FCSTD DOCUMENT  (FreeCAD 0.20R29177 +426 (Git))
Label: RecogBoxPartialAssembly_v3
License: All rights reserved
LicenseURL: https://en.wikipedia.org/wiki/All_rights_reserved
objects: App::DocumentObjectGroup×4, App::Link×3, PartDesign::CoordinateSystem×1, App::FeaturePython×1, App::Part×1, Part::FeaturePython×1, App::AnnotationLabel×1
note: 2 computed .brp shape members not serialized (recipe doc carries the construction recipe); baked Part::Feature solids carry a one-line shape summary decoded from their .brp
EXTERNAL_REF file=ImageRecogBox-v3-cutinparts.FCStd obj=LCS_2
EXTERNAL_REF file=ImageRecogBox-v3-cutinparts.FCStd obj=Body
EXTERNAL_REF file=ImageRecogBox-v3-cutinparts.FCStd obj=LCS_6
EXTERNAL_REF file=left_handle.FCStd obj=LCS_1
EXTERNAL_REF file=left_handle.FCStd obj=Body
EXTERNAL_REF file=ImageRecogBox-v3-cutinparts.FCStd obj=LCS_5
EXTERNAL_REF file=right_handle.FCStd obj=LCS_1
EXTERNAL_REF file=right_handle.FCStd obj=Body

FEATURE [App::DocumentObjectGroup] Parts
FEATURE [PartDesign::CoordinateSystem] LCS_Origin
  AttacherType = Attacher::AttachEngine3D
  MapMode = 2
  Support = -> [X_Axis]
FEATURE [App::DocumentObjectGroup] Constraints
FEATURE [App::FeaturePython] Variables  # WARN: FeaturePython — macro-defined, semantics opaque (R4)
  Type = App::PropertyContainer
FEATURE [App::DocumentObjectGroup] Configurations
FEATURE [App::Link] ImageRecogBox_body  label="ImageRecogBox-body"
  AttachedBy = #LCS_2
  AttachedTo = Parent Assembly#LCS_Origin
  LinkedObject = -> <external ImageRecogBox-v3-cutinparts.FCStd>#Body
  SolverId = Asm4EE
  expr: Placement = LCS_Origin.Placement * AttachmentOffset * ImageRecogBox_v3_cutinparts#LCS_2.Placement ^ -1
FEATURE [App::Link] Body
  AttachedBy = #LCS_1
  AttachedTo = ImageRecogBox_body#LCS_6
  LinkPlacement = pos=(-121.969,50.5,41.5) rot=(0,0,-1;1.5708rad)
  LinkedObject = -> <external left_handle.FCStd>#Body
  Placement = pos=(-121.969,50.5,41.5) rot=(0,0,-1;1.5708rad)
  SolverId = Asm4EE
  expr: Placement = ImageRecogBox_body.Placement * ImageRecogBox_v3_cutinparts#LCS_6.Placement * AttachmentOffset * left_handle#LCS_1.Placement ^ -1
FEATURE [App::Link] Body001
  AttachedBy = #LCS_1
  AttachedTo = ImageRecogBox_body#LCS_5
  LinkPlacement = pos=(17.25,130.878,41.5) rot=(0,0,-1;0.523599rad)
  LinkedObject = -> <external right_handle.FCStd>#Body
  Placement = pos=(17.25,130.878,41.5) rot=(0,0,-1;0.523599rad)
  SolverId = Asm4EE
  expr: Placement = ImageRecogBox_body.Placement * ImageRecogBox_v3_cutinparts#LCS_5.Placement * AttachmentOffset * right_handle#LCS_1.Placement ^ -1
FEATURE [App::Part] Assembly
  AssemblyType = Part::Link
  Group = -> [LCS_Origin,Constraints,Variables,Configurations,ImageRecogBox_body,Body,Body001]
  Origin = -> Origin
  Type = Assembly
FEATURE [Part::FeaturePython] DistPoints  # WARN: FeaturePython — macro-defined, semantics opaque (R4)
FEATURE [App::AnnotationLabel] MeasureLbl
  BasePosition = (-78.861,136.591,41.5)
  LabelText = D = 33,36 mm
  TextPosition = (0,0,0)
FEATURE [App::DocumentObjectGroup] Measures
  Group = -> [DistPoints,MeasureLbl]

RESOLVED EXTERNAL PARTS (link-assembly join: the EXTERNAL_REF files above that resolve inside this repo's crawl, each included once):
---- part ImageRecogBox-v3-cutinparts.FCStd = doc fcstd_85f84b476632 ----
FCSTD DOCUMENT  (FreeCAD 0.20R29177 +426 (Git))
Label: ImageRecogBox-v3-cutinparts
License: All rights reserved
LicenseURL: http://en.wikipedia.org/wiki/All_rights_reserved
objects: Sketcher::SketchObject×16, PartDesign::Pad×9, PartDesign::CoordinateSystem×6, PartDesign::Hole×4, PartDesign::Pocket×3, PartDesign::Chamfer×2, App::DocumentObjectGroup×1, PartDesign::Body×1
note: 59 computed .brp shape members not serialized (recipe doc carries the construction recipe); baked Part::Feature solids carry a one-line shape summary decoded from their .brp

FEATURE [Sketcher::SketchObject] Sketch
  FullyConstrained = true
  MapMode = 5
  Support = -> [XY_Plane]
  sketch-geometry (14):
    g0: LineSegment StartX=86.6025 StartY=50 StartZ=0 EndX=0 EndY=100 EndZ=0
    g1: LineSegment StartX=4.3e-15 StartY=100 StartZ=0 EndX=-86.6025 EndY=50 EndZ=0
    g2: LineSegment StartX=-86.6025 StartY=50 StartZ=0 EndX=-86.6025 EndY=-50 EndZ=0
    g3: LineSegment StartX=-86.6025 StartY=-50 StartZ=0 EndX=0 EndY=-100 EndZ=0
    g4: LineSegment StartX=0 StartY=-100 StartZ=0 EndX=86.6025 EndY=-50 EndZ=0
    g5: LineSegment StartX=86.6025 StartY=-50 StartZ=0 EndX=86.6025 EndY=50 EndZ=0
    g6: Circle CenterX=0 CenterY=0 CenterZ=0 NormalX=0 NormalY=0 NormalZ=1 AngleXU=0 Radius=100
    g7: LineSegment StartX=87.4686 StartY=-50.5 StartZ=0 EndX=87.4686 EndY=50.5 EndZ=0
    g8: LineSegment StartX=87.4686 StartY=50.5 StartZ=0 EndX=-1.42e-14 EndY=101 EndZ=0
    g9: LineSegment StartX=-1.48e-14 StartY=101 StartZ=0 EndX=-87.4686 EndY=50.5 EndZ=0
    g10: LineSegment StartX=-87.4686 StartY=50.5 StartZ=0 EndX=-87.4686 EndY=-50.5 EndZ=0
    g11: LineSegment StartX=-87.4686 StartY=-50.5 StartZ=0 EndX=0 EndY=-101 EndZ=0
    g12: LineSegment StartX=0 StartY=-101 StartZ=0 EndX=87.4686 EndY=-50.5 EndZ=0
    g13: Circle CenterX=0 CenterY=0 CenterZ=0 NormalX=0 NormalY=0 NormalZ=1 AngleXU=0 Radius=101
  constraints (33):
    c: Coincident(g0,g1)
    c: Coincident(g1,g2)
    c: Coincident(g2,g3)
    c: Coincident(g3,g4)
    c: Coincident(g4,g5)
    c: Coincident(g5,g0)
    c: Equal(g0, g1-g5) x5
    c: PointOnObject(g0,g6)
    c: PointOnObject(g1,g6)
    c: PointOnObject(g2,g6)
    c: PointOnObject(g3,g6)
    c: PointOnObject(g4,g6)
    c: PointOnObject(g5,g6)
    c: Coincident(g6,g-1)
    c: Vertical(g5)
    c: Coincident(g7,g8)
    c: Coincident(g8,g9)
    c: Coincident(g9,g10)
    c: Coincident(g10,g11)
    c: Coincident(g11,g12)
    c: Coincident(g12,g7)
    c: Equal(g7, g8-g12) x5
    c: PointOnObject(g7,g13)
    c: PointOnObject(g8,g13)
    c: PointOnObject(g9,g13)
    c: PointOnObject(g10,g13)
    c: PointOnObject(g11,g13)
    c: PointOnObject(g12,g13)
    c: Coincident(g13,g6)
    c: Vertical(g7)
    c: Diameter(g6) = 200
    c: DistanceY(g5,g5) = 100
    c: Diameter(g13) = 202
FEATURE [PartDesign::Pad] Pad
  Direction = (0,0,1)
  Length = 150
  Length2 = 10
  Profile = -> Sketch
  ReferenceAxis = -> Sketch [N_Axis]
  Type = 0
FEATURE [Sketcher::SketchObject] Sketch001
  ExternalGeometry = -> [Pad]
  FullyConstrained = true
  MapMode = 5
  Placement = pos=(0,0,0) rot=(1,0,0;3.14159rad)
  Support = -> [Pad]
  sketch-geometry (4):
    g0: LineSegment StartX=103.603 StartY=0 StartZ=0 EndX=86.6025 EndY=0 EndZ=0
    g1: LineSegment StartX=86.6025 StartY=0 StartZ=0 EndX=86.6025 EndY=-10 EndZ=0
    g2: LineSegment StartX=86.6025 StartY=-10 StartZ=0 EndX=103.603 EndY=-10 EndZ=0
    g3: LineSegment StartX=103.603 StartY=-10 StartZ=0 EndX=103.603 EndY=0 EndZ=0
  constraints (12):
    c: Coincident(g0,g1)
    c: Coincident(g1,g2)
    c: Coincident(g2,g3)
    c: Coincident(g3,g0)
    c: Horizontal(g0)
    c: Horizontal(g2)
    c: Vertical(g1)
    c: Vertical(g3)
    c: PointOnObject(g1,g-3)
    c: DistanceX(g2,g2) = 17
    c: DistanceY(g3,g3) = 10
    c: PointOnObject(g0,g-1)
FEATURE [PartDesign::Pad] Pad001
  BaseFeature = -> Pad
  Direction = (0,0,-1)
  Length = 25
  Length2 = 10
  Profile = -> Sketch001
  ReferenceAxis = -> Sketch001 [N_Axis]
  Type = 0
FEATURE [Sketcher::SketchObject] Sketch002
  ExternalGeometry = -> [Pad001]
  FullyConstrained = true
  MapMode = 5
  Placement = pos=(0,0,-25) rot=(1,0,0;3.14159rad)
  Support = -> [Pad001]
  sketch-geometry (4):
    g0: LineSegment StartX=103.603 StartY=-10 StartZ=0 EndX=73.6025 EndY=-10 EndZ=0
    g1: LineSegment StartX=73.6025 StartY=-10 StartZ=0 EndX=73.6025 EndY=50 EndZ=0
    g2: LineSegment StartX=73.6025 StartY=50 StartZ=0 EndX=103.603 EndY=50 EndZ=0
    g3: LineSegment StartX=103.603 StartY=50 StartZ=0 EndX=103.603 EndY=-10 EndZ=0
  constraints (11):
    c: Coincident(g0,g1)
    c: Coincident(g2,g3)
    c: Coincident(g3,g0)
    c: Horizontal(g0)
    c: Vertical(g3)
    c: Coincident(g0,g-4)
    c: Coincident(g2,g1)
    c: Horizontal(g2)
    c: Horizontal(g2,g-6)
    c: Vertical(g1)
    c: DistanceX(g0,g0) = 30
FEATURE [PartDesign::Pad] Pad002
  BaseFeature = -> Pad001
  Direction = (0,0,-1)
  Length = 8
  Length2 = 10
  Profile = -> Sketch002
  ReferenceAxis = -> Sketch002 [N_Axis]
  Type = 0
FEATURE [Sketcher::SketchObject] Sketch003
  ExternalGeometry = -> [Pad002]
  FullyConstrained = true
  MapMode = 5
  Placement = pos=(0,0,-25) rot=(0,0,1;0rad)
  Support = -> [Pad002]
  sketch-geometry (6):
    g0: LineSegment StartX=76.1025 StartY=-8 StartZ=0 EndX=89.1025 EndY=-8 EndZ=0
    g1: LineSegment StartX=89.1025 StartY=-8 StartZ=0 EndX=89.1025 EndY=-32 EndZ=0
    g2: LineSegment StartX=89.1025 StartY=-32 StartZ=0 EndX=76.1025 EndY=-32 EndZ=0
    g3: LineSegment StartX=76.1025 StartY=-32 StartZ=0 EndX=76.1025 EndY=-8 EndZ=0
    g4: GeomPoint X=82.6025 Y=-20 Z=0
    g5: GeomPoint X=88.6025 Y=-20 Z=0
  constraints (14):
    c: Coincident(g0,g1)
    c: Coincident(g1,g2)
    c: Coincident(g2,g3)
    c: Coincident(g3,g0)
    c: Horizontal(g0)
    c: Horizontal(g2)
    c: Vertical(g1)
    c: Vertical(g3)
    c: DistanceY(g1,g1) = 24
    c: DistanceX(g2,g2) = 13
    c: Symmetric(g1,g0,g4)
    c: Symmetric(g-5,g-3,g5)
    c: DistanceX(g4,g5) = 6
    c: Horizontal(g5,g4)
FEATURE [PartDesign::Pocket] Pocket
  BaseFeature = -> Pad002
  Direction = (0,0,-1)
  Length = 19
  Length2 = 5
  Profile = -> Sketch003
  ReferenceAxis = -> Sketch003 [N_Axis]
  Type = 1
FEATURE [Sketcher::SketchObject] Sketch004
  ExternalGeometry = -> [Pocket]
  FullyConstrained = false
  MapMode = 5
  Placement = pos=(0,0,-25) rot=(0,0,1;0rad)
  Support = -> [Pocket]
  sketch-geometry (5):
    g0: GeomPoint X=82.6025 Y=-6.3796 Z=0
    g1: GeomPoint X=82.6025 Y=-33.3796 Z=0
    g2: Circle CenterX=82.6025 CenterY=-6.3796 CenterZ=0 NormalX=0 NormalY=0 NormalZ=1 AngleXU=0 Radius=1
    g3: Circle CenterX=82.6025 CenterY=-33.3796 CenterZ=0 NormalX=0 NormalY=0 NormalZ=1 AngleXU=0 Radius=1
    g4: GeomPoint X=82.6025 Y=-20 Z=0
  constraints (8):
    c: DistanceY(g1,g0) = 27
    c: Coincident(g2,g0)
    c: Coincident(g3,g1)
    c: Equal(g3,g2)
    c: Diameter(g2) = 2
    c: Symmetric(g-6,g-5,g4)
    c: Vertical(g2,g3)
    c: Vertical(g3,g4)
FEATURE [PartDesign::Hole] Hole
  BaseFeature = -> Pocket
  CustomThreadClearance = 0
  Depth = 25
  DepthType = 0
  Diameter = 1.6
  DrillForDepth = false
  DrillPoint = 1
  DrillPointAngle = 118
  HoleCutCountersinkAngle = 90
  HoleCutCustomValues = false
  HoleCutDepth = 0
  HoleCutDiameter = 6.1
  HoleCutType = 0
  ModelThread = false
  Profile = -> Sketch004
  Tapered = false
  TaperedAngle = 90
  ThreadClass = 0
  ThreadDepth = 25
  ThreadDepthType = 0
  ThreadDirection = 0
  ThreadFit = 0
  ThreadSize = 6
  ThreadType = 1
  Threaded = true
  UseCustomThreadClearance = false
FEATURE [PartDesign::CoordinateSystem] LCS_1
  AttacherType = Attacher::AttachEngine3D
  MapMode = 45
  Placement = pos=(82.6025,-6.3796,-25) rot=(0,0,1;0rad)
  Support = -> [Hole]
FEATURE [PartDesign::CoordinateSystem] LCS_2  label="LCS_origin"
  AttacherType = Attacher::AttachEngine3D
FEATURE [PartDesign::Chamfer] Chamfer
  Angle = 45
  Base = -> Hole [Edge4]
  BaseFeature = -> Hole
  ChamferType = 0
  FlipDirection = false
  Size = 16
  Size2 = 1
  SupportTransform = false
  UseAllEdges = false
FEATURE [PartDesign::Chamfer] Chamfer001
  Angle = 45
  Base = -> Chamfer [Edge12,Edge49]
  BaseFeature = -> Chamfer
  ChamferType = 0
  FlipDirection = false
  Size = 3
  Size2 = 1
  SupportTransform = false
  UseAllEdges = false
FEATURE [Sketcher::SketchObject] Sketch005
  ExternalGeometry = -> [Chamfer001]
  FullyConstrained = true
  MapMode = 5
  Placement = pos=(0,0,0) rot=(1,0,0;3.14159rad)
  Support = -> [Chamfer001]
  sketch-geometry (8):
    g0: LineSegment StartX=86.6025 StartY=-10 StartZ=0 EndX=86.6025 EndY=-50 EndZ=0
    g1: LineSegment StartX=86.6025 StartY=-50 StartZ=0 EndX=0 EndY=-100 EndZ=0
    g2: LineSegment StartX=0 StartY=-100 StartZ=0 EndX=-86.6025 EndY=-50 EndZ=0
    g3: LineSegment StartX=-86.6025 StartY=-50 StartZ=0 EndX=-87.4686 EndY=-50.5 EndZ=0
    g4: LineSegment StartX=-87.4686 StartY=-50.5 StartZ=0 EndX=-1.42e-14 EndY=-101 EndZ=0
    g5: LineSegment StartX=-1.42e-14 StartY=-101 StartZ=0 EndX=87.4686 EndY=-50.5 EndZ=0
    g6: LineSegment StartX=87.4686 StartY=-50.5 StartZ=0 EndX=87.4686 EndY=-10 EndZ=0
    g7: LineSegment StartX=87.4686 StartY=-10 StartZ=0 EndX=86.6025 EndY=-10 EndZ=0
  constraints (16):
    c: Coincident(g-7,g0)
    c: Coincident(g0,g-7)
    c: Coincident(g0,g1)
    c: Coincident(g1,g-4)
    c: Coincident(g1,g2)
    c: Coincident(g2,g-3)
    c: Coincident(g2,g3)
    c: Coincident(g3,g-5)
    c: Coincident(g3,g4)
    c: Coincident(g4,g-6)
    c: Coincident(g4,g5)
    c: Coincident(g5,g-8)
    c: Coincident(g5,g6)
    c: Coincident(g6,g-8)
    c: Coincident(g6,g7)
    c: Coincident(g7,g0)
FEATURE [PartDesign::Pad] Pad003
  BaseFeature = -> Chamfer001
  Direction = (0,0,-1)
  Length = 12
  Length2 = 10
  Profile = -> Sketch005
  ReferenceAxis = -> Sketch005 [N_Axis]
  Type = 0
FEATURE [Sketcher::SketchObject] Sketch006
  ExternalGeometry = -> [Pad003]
  FullyConstrained = true
  MapMode = 5
  Placement = pos=(87.4686,0,0) rot=(0.57735,0.57735,0.57735;2.0944rad)
  Support = -> [Pad003]
  sketch-geometry (6):
    g0: GeomPoint X=30.25 Y=-12 Z=0
    g1: LineSegment StartX=37.75 StartY=-12 StartZ=0 EndX=22.75 EndY=-12 EndZ=0
    g2: LineSegment StartX=22.75 StartY=-12 StartZ=0 EndX=22.75 EndY=38 EndZ=0
    g3: LineSegment StartX=22.75 StartY=38 StartZ=0 EndX=37.75 EndY=38 EndZ=0
    g4: LineSegment StartX=37.75 StartY=38 StartZ=0 EndX=37.75 EndY=-12 EndZ=0
    g5: GeomPoint X=22.75 Y=13 Z=0
  constraints (13):
    c: Symmetric(g-3,g-3,g0)
    c: Coincident(g1,g2)
    c: Coincident(g2,g3)
    c: Coincident(g3,g4)
    c: Coincident(g4,g1)
    c: Horizontal(g1)
    c: Horizontal(g3)
    c: Vertical(g2)
    c: Vertical(g4)
    c: Symmetric(g1,g1,g0)
    c: DistanceX(g1,g1) = 15
    c: DistanceY(g4,g4) = 50
    c: Symmetric(g2,g1,g5)
FEATURE [PartDesign::Pad] Pad004
  BaseFeature = -> Pad003
  Direction = (1,0,0)
  Length = 10
  Length2 = 10
  Profile = -> Sketch006
  ReferenceAxis = -> Sketch006 [N_Axis]
  Type = 0
FEATURE [Sketcher::SketchObject] Sketch007
  ExternalGeometry = -> [Pad004]
  FullyConstrained = false
  MapMode = 5
  Placement = pos=(97.4686,0,0) rot=(0.57735,0.57735,0.57735;2.0944rad)
  Support = -> [Pad004]
  sketch-geometry (3):
    g0: Circle CenterX=30.25 CenterY=25.5 CenterZ=0 NormalX=0 NormalY=0 NormalZ=1 AngleXU=0 Radius=1.58506
    g1: GeomPoint X=22.75 Y=13 Z=0
    g2: Circle CenterX=30.25 CenterY=0.5 CenterZ=0 NormalX=0 NormalY=0 NormalZ=1 AngleXU=0 Radius=1.58506
  constraints (3):
    c: Symmetric(g-3,g-3,g1)
    c: Symmetric(g-4,g1,g0)
    c: Symmetric(g-4,g1,g2)
FEATURE [PartDesign::Hole] Hole001
  BaseFeature = -> Pad004
  CustomThreadClearance = 0
  Depth = 6
  DepthType = 0
  Diameter = 3.4
  DrillForDepth = false
  DrillPoint = 1
  DrillPointAngle = 118
  HoleCutCountersinkAngle = 90
  HoleCutCustomValues = false
  HoleCutDepth = 0
  HoleCutDiameter = 6.1
  HoleCutType = 0
  ModelThread = false
  Profile = -> Sketch007
  Tapered = false
  TaperedAngle = 90
  ThreadClass = 0
  ThreadDepth = 6
  ThreadDepthType = 0
  ThreadDirection = 0
  ThreadFit = 0
  ThreadSize = 9
  ThreadType = 1
  Threaded = false
  UseCustomThreadClearance = false
FEATURE [PartDesign::CoordinateSystem] LCS_3
  AttacherType = Attacher::AttachEngine3D
  MapMode = 11
  Placement = pos=(97.4686,30.25,25.5) rot=(0.57735,0.57735,0.57735;2.0944rad)
  Support = -> [Hole001]
FEATURE [App::DocumentObjectGroup] Measures
FEATURE [Sketcher::SketchObject] Sketch008
  ExternalGeometry = -> [Hole001]
  FullyConstrained = true
  MapMode = 5
  Placement = pos=(43.7343,75.75,0) rot=(0.186157,0.694747,0.694747;2.77349rad)
  Support = -> [Hole001]
  sketch-geometry (5):
    g0: GeomPoint X=-2.7e-15 Y=-12 Z=0
    g1: LineSegment StartX=-7.5 StartY=38 StartZ=0 EndX=7.5 EndY=38 EndZ=0
    g2: LineSegment StartX=7.5 StartY=38 StartZ=0 EndX=7.5 EndY=-12 EndZ=0
    g3: LineSegment StartX=7.5 StartY=-12 StartZ=0 EndX=-7.5 EndY=-12 EndZ=0
    g4: LineSegment StartX=-7.5 StartY=-12 StartZ=0 EndX=-7.5 EndY=38 EndZ=0
  constraints (12):
    c: Symmetric(g-3,g-3,g0)
    c: Coincident(g1,g2)
    c: Coincident(g2,g3)
    c: Coincident(g3,g4)
    c: Coincident(g4,g1)
    c: Horizontal(g1)
    c: Horizontal(g3)
    c: Vertical(g2)
    c: Vertical(g4)
    c: DistanceX(g1,g1) = 15
    c: DistanceY(g2,g2) = 50
    c: Symmetric(g3,g2,g0)
FEATURE [PartDesign::Pad] Pad005
  BaseFeature = -> Hole001
  Direction = (0.5,0.866025,-1e-16)
  Length = 10
  Length2 = 10
  Profile = -> Sketch008
  ReferenceAxis = -> Sketch008 [N_Axis]
  Type = 0
FEATURE [Sketcher::SketchObject] Sketch009
  ExternalGeometry = -> [Pad005]
  FullyConstrained = false
  MapMode = 5
  Placement = pos=(48.7343,84.4103,0) rot=(0.186157,0.694747,0.694747;2.77349rad)
  Support = -> [Pad005]
  sketch-geometry (3):
    g0: Circle CenterX=-1.06e-14 CenterY=25.5 CenterZ=0 NormalX=0 NormalY=0 NormalZ=1 AngleXU=0 Radius=1.89055
    g1: GeomPoint X=-7.5 Y=13 Z=0
    g2: Circle CenterX=-1.04e-14 CenterY=0.5 CenterZ=0 NormalX=0 NormalY=0 NormalZ=1 AngleXU=0 Radius=1.89055
  constraints (3):
    c: Symmetric(g-3,g-4,g1)
    c: Symmetric(g-3,g1,g0)
    c: Symmetric(g1,g-4,g2)
FEATURE [PartDesign::Hole] Hole002
  BaseFeature = -> Pad005
  CustomThreadClearance = 0
  Depth = 6
  DepthType = 0
  Diameter = 3.4
  DrillForDepth = false
  DrillPoint = 1
  DrillPointAngle = 118
  HoleCutCountersinkAngle = 90
  HoleCutCustomValues = false
  HoleCutDepth = 0
  HoleCutDiameter = 6.1
  HoleCutType = 0
  ModelThread = false
  Profile = -> Sketch009
  Tapered = false
  TaperedAngle = 90
  ThreadClass = 0
  ThreadDepth = 6
  ThreadDepthType = 0
  ThreadDirection = 0
  ThreadFit = 0
  ThreadSize = 9
  ThreadType = 1
  Threaded = false
  UseCustomThreadClearance = false
FEATURE [Sketcher::SketchObject] Sketch010
  ExternalGeometry = -> [Hole002]
  FullyConstrained = true
  MapMode = 5
  Placement = pos=(-43.7343,75.75,0) rot=(-0.186157,0.694747,0.694747;3.50969rad)
  Support = -> [Hole002]
  sketch-geometry (5):
    g0: GeomPoint X=5.6e-15 Y=-12 Z=0
    g1: LineSegment StartX=-7.5 StartY=-12 StartZ=0 EndX=7.5 EndY=-12 EndZ=0
    g2: LineSegment StartX=7.5 StartY=-12 StartZ=0 EndX=7.5 EndY=38 EndZ=0
    g3: LineSegment StartX=7.5 StartY=38 StartZ=0 EndX=-7.5 EndY=38 EndZ=0
    g4: LineSegment StartX=-7.5 StartY=38 StartZ=0 EndX=-7.5 EndY=-12 EndZ=0
  constraints (12):
    c: Symmetric(g-3,g-3,g0)
    c: Coincident(g1,g2)
    c: Coincident(g2,g3)
    c: Coincident(g3,g4)
    c: Coincident(g4,g1)
    c: Horizontal(g1)
    c: Horizontal(g3)
    c: Vertical(g2)
    c: Vertical(g4)
    c: Symmetric(g1,g1,g0)
    c: DistanceY(g2,g2) = 50
    c: DistanceX(g3,g3) = 15
FEATURE [PartDesign::Pad] Pad006
  BaseFeature = -> Hole002
  Direction = (-0.5,0.866025,0)
  Length = 10
  Length2 = 10
  Profile = -> Sketch010
  ReferenceAxis = -> Sketch010 [N_Axis]
  Type = 0
FEATURE [Sketcher::SketchObject] Sketch011
  ExternalGeometry = -> [Pad006]
  FullyConstrained = false
  MapMode = 5
  Placement = pos=(-48.7343,84.4103,0) rot=(-0.186157,0.694747,0.694747;3.50969rad)
  Support = -> [Pad006]
  sketch-geometry (3):
    g0: GeomPoint X=-7.5 Y=13 Z=0
    g1: Circle CenterX=3.62e-14 CenterY=25.5 CenterZ=0 NormalX=0 NormalY=0 NormalZ=1 AngleXU=0 Radius=1.24684
    g2: Circle CenterX=3.54e-14 CenterY=0.5 CenterZ=0 NormalX=0 NormalY=0 NormalZ=1 AngleXU=0 Radius=1.24684
  constraints (3):
    c: Symmetric(g-3,g-4,g0)
    c: Symmetric(g-3,g0,g1)
    c: Symmetric(g-4,g0,g2)
FEATURE [PartDesign::Hole] Hole003
  BaseFeature = -> Pad006
  CustomThreadClearance = 0
  Depth = 6
  DepthType = 0
  Diameter = 3.4
  DrillForDepth = false
  DrillPoint = 1
  DrillPointAngle = 118
  HoleCutCountersinkAngle = 90
  HoleCutCustomValues = false
  HoleCutDepth = 0
  HoleCutDiameter = 6.1
  HoleCutType = 0
  ModelThread = false
  Profile = -> Sketch011
  Tapered = false
  TaperedAngle = 90
  ThreadClass = 0
  ThreadDepth = 6
  ThreadDepthType = 0
  ThreadDirection = 0
  ThreadFit = 0
  ThreadSize = 9
  ThreadType = 1
  Threaded = false
  UseCustomThreadClearance = false
FEATURE [Sketcher::SketchObject] Sketch012
  ExternalGeometry = -> [Hole003]
  FullyConstrained = true
  MapMode = 5
  Placement = pos=(-87.4686,-1.22e-14,0) rot=(0.57735,-0.57735,-0.57735;2.0944rad)
  Support = -> [Hole003]
  sketch-geometry (4):
    g0: LineSegment StartX=-50.5 StartY=55 StartZ=0 EndX=50.5 EndY=55 EndZ=0
    g1: LineSegment StartX=50.5 StartY=55 StartZ=0 EndX=50.5 EndY=40 EndZ=0
    g2: LineSegment StartX=50.5 StartY=40 StartZ=0 EndX=-50.5 EndY=40 EndZ=0
    g3: LineSegment StartX=-50.5 StartY=40 StartZ=0 EndX=-50.5 EndY=55 EndZ=0
  constraints (12):
    c: Coincident(g0,g1)
    c: Coincident(g1,g2)
    c: Coincident(g2,g3)
    c: Coincident(g3,g0)
    c: Horizontal(g0)
    c: Horizontal(g2)
    c: Vertical(g1)
    c: Vertical(g3)
    c: PointOnObject(g0,g-3)
    c: PointOnObject(g0,g-4)
    c: DistanceY(g1,g1) = 15
    c: DistanceY(g-4,g2) = 40
FEATURE [PartDesign::Pad] Pad007
  BaseFeature = -> Hole003
  Direction = (-1,-1e-16,-1e-16)
  Length = 15
  Length2 = 10
  Profile = -> Sketch012
  ReferenceAxis = -> Sketch012 [N_Axis]
  Type = 0
FEATURE [Sketcher::SketchObject] Sketch013
  ExternalGeometry = -> [Pad007]
  FullyConstrained = true
  MapMode = 5
  Placement = pos=(-5.6e-15,50.5,5.6e-15) rot=(0,0.707107,0.707107;3.14159rad)
  Support = -> [Pad007]
  sketch-geometry (5):
    g0: LineSegment StartX=88.9686 StartY=53.5 StartZ=0 EndX=88.9686 EndY=41.5 EndZ=0
    g1: LineSegment StartX=88.9686 StartY=41.5 StartZ=0 EndX=100.969 EndY=41.5 EndZ=0
    g2: LineSegment StartX=100.969 StartY=41.5 StartZ=0 EndX=100.969 EndY=53.5 EndZ=0
    g3: LineSegment StartX=100.969 StartY=53.5 StartZ=0 EndX=88.9686 EndY=53.5 EndZ=0
    g4: GeomPoint X=94.9686 Y=47.5 Z=0
  constraints (12):
    c: Coincident(g0,g1)
    c: Coincident(g1,g2)
    c: Coincident(g2,g3)
    c: Coincident(g3,g0)
    c: Horizontal(g1)
    c: Horizontal(g3)
    c: Vertical(g0)
    c: Vertical(g2)
    c: Symmetric(g1,g0,g4)
    c: Equal(g3,g2)
    c: Symmetric(g-4,g-5,g4)
    c: DistanceX(g3,g3) = 12
FEATURE [PartDesign::Pocket] Pocket001
  BaseFeature = -> Pad007
  Direction = (1e-16,-1,-2e-16)
  Length = 5
  Length2 = 5
  Profile = -> Sketch013
  ReferenceAxis = -> Sketch013 [N_Axis]
  Type = 1
FEATURE [Sketcher::SketchObject] Sketch014
  ExternalGeometry = -> [Pocket001]
  FullyConstrained = true
  MapMode = 5
  Placement = pos=(43.7343,75.75,0) rot=(0.186157,0.694747,0.694747;2.77349rad)
  Support = -> [Pocket001]
  sketch-geometry (4):
    g0: LineSegment StartX=-50.5 StartY=55 StartZ=0 EndX=50.5 EndY=55 EndZ=0
    g1: LineSegment StartX=50.5 StartY=55 StartZ=0 EndX=50.5 EndY=40 EndZ=0
    g2: LineSegment StartX=50.5 StartY=40 StartZ=0 EndX=-50.5 EndY=40 EndZ=0
    g3: LineSegment StartX=-50.5 StartY=40 StartZ=0 EndX=-50.5 EndY=55 EndZ=0
  constraints (12):
    c: Coincident(g0,g1)
    c: Coincident(g1,g2)
    c: Coincident(g2,g3)
    c: Coincident(g3,g0)
    c: Horizontal(g0)
    c: Horizontal(g2)
    c: Vertical(g1)
    c: Vertical(g3)
    c: PointOnObject(g1,g-3)
    c: PointOnObject(g2,g-4)
    c: DistanceY(g-3,g1) = 40
    c: DistanceY(g1,g1) = 15
FEATURE [PartDesign::Pad] Pad008
  BaseFeature = -> Pocket001
  Direction = (0.5,0.866025,-1e-16)
  Length = 15
  Length2 = 10
  Profile = -> Sketch014
  ReferenceAxis = -> Sketch014 [N_Axis]
  Refine = true
  Type = 0
FEATURE [Sketcher::SketchObject] Sketch015
  ExternalGeometry = -> [Pad008]
  FullyConstrained = true
  MapMode = 5
  Placement = pos=(-43.7343,25.25,-1.5e-15) rot=(-0.377964,0.654654,0.654654;3.86433rad)
  Support = -> [Pad008]
  sketch-geometry (5):
    g0: LineSegment StartX=-100.969 StartY=53.5 StartZ=0 EndX=-100.969 EndY=41.5 EndZ=0
    g1: LineSegment StartX=-100.969 StartY=41.5 StartZ=0 EndX=-88.9686 EndY=41.5 EndZ=0
    g2: LineSegment StartX=-88.9686 StartY=41.5 StartZ=0 EndX=-88.9686 EndY=53.5 EndZ=0
    g3: LineSegment StartX=-88.9686 StartY=53.5 StartZ=0 EndX=-100.969 EndY=53.5 EndZ=0
    g4: GeomPoint X=-94.9686 Y=47.5 Z=0
  constraints (12):
    c: Coincident(g0,g1)
    c: Coincident(g1,g2)
    c: Coincident(g2,g3)
    c: Coincident(g3,g0)
    c: Horizontal(g1)
    c: Horizontal(g3)
    c: Vertical(g0)
    c: Vertical(g2)
    c: Symmetric(g1,g0,g4)
    c: DistanceX(g3,g3) = 12
    c: Equal(g2,g3)
    c: Symmetric(g-4,g-3,g4)
FEATURE [PartDesign::Pocket] Pocket002
  BaseFeature = -> Pad008
  Direction = (0.866025,-0.5,-1e-16)
  Length = 5
  Length2 = 5
  Profile = -> Sketch015
  ReferenceAxis = -> Sketch015 [N_Axis]
  Refine = true
  Type = 1
FEATURE [PartDesign::CoordinateSystem] LCS_4
  AttacherType = Attacher::AttachEngine3D
FEATURE [PartDesign::CoordinateSystem] LCS_5  label="rightHandleLCS"
  AttacherType = Attacher::AttachEngine3D
  AttachmentOffset = pos=(0,0,-12) rot=(1,0,0;1.5708rad)
  MapMode = 7
  Placement = pos=(0.75,102.299,41.5) rot=(0.258819,0.965926,0;3.14159rad)
  Support = -> [Pocket002]
FEATURE [PartDesign::CoordinateSystem] LCS_6  label="leftHandleLCS"
  AttacherType = Attacher::AttachEngine3D
  AttachmentOffset = pos=(0,0,0) rot=(1,0,0;1.5708rad)
  MapMode = 7
  Placement = pos=(-88.9686,50.5,41.5) rot=(0.707107,0.707107,0;3.14159rad)
  Support = -> [Pocket002]
FEATURE [PartDesign::Body] Body  label="ImageRecogBox-body"
  Group = -> [Sketch,Pad,Sketch001,Pad001,Sketch002,Pad002,Sketch003,Pocket,Sketch004,Hole,LCS_1,LCS_2,Chamfer,Chamfer001,Sketch005,Pad003,Sketch006,Pad004,Sketch007,Hole001,LCS_3,Sketch008,Pad005,Sketch009,Hole002,Sketch010,Pad006,Sketch011,Hole003,Sketch012,Pad007,Sketch013,Pocket001,Sketch014,Pad008,Sketch015,Pocket002,LCS_4,LCS_5,LCS_6]
  Origin = -> Origin
  Tip = -> Pocket002
---- part left_handle.FCStd = doc fcstd_5dd48c4c5e5f ----
FCSTD DOCUMENT  (FreeCAD 0.20R29177 +426 (Git))
Label: left_handle
License: All rights reserved
LicenseURL: http://en.wikipedia.org/wiki/All_rights_reserved
objects: Sketcher::SketchObject×7, PartDesign::Pad×3, PartDesign::Pocket×2, PartDesign::SubShapeBinder×1, PartDesign::CoordinateSystem×1, PartDesign::Body×1
note: 20 computed .brp shape members not serialized (recipe doc carries the construction recipe); baked Part::Feature solids carry a one-line shape summary decoded from their .brp

FEATURE [Sketcher::SketchObject] Sketch  label="master"
  FullyConstrained = true
  MapMode = 5
  Support = -> [XY_Plane]
  sketch-geometry (15):
    g0: LineSegment StartX=-107.866 StartY=40.8218 StartZ=0 EndX=-84.297 EndY=0 EndZ=0
    g1: LineSegment StartX=-84.297 StartY=0 StartZ=0 EndX=80 EndY=0 EndZ=0
    g2: LineSegment StartX=80 StartY=0 StartZ=0 EndX=80 EndY=20 EndZ=0
    g3: LineSegment StartX=80 StartY=20 StartZ=0 EndX=0 EndY=20 EndZ=0
    g4: LineSegment StartX=-72.75 StartY=20 StartZ=0 EndX=-90.545 EndY=50.8218 EndZ=0
    g5: LineSegment StartX=-90.545 StartY=50.8218 StartZ=0 EndX=-107.866 EndY=40.8218 EndZ=0
    g6: GeomPoint X=0 Y=20 Z=0
    g7: LineSegment StartX=-5 StartY=20 StartZ=0 EndX=-5 EndY=35 EndZ=0
    g8: LineSegment StartX=-5 StartY=35 StartZ=0 EndX=0 EndY=35 EndZ=0
    g9: LineSegment StartX=0 StartY=35 StartZ=0 EndX=0 EndY=33 EndZ=0
    g10: LineSegment StartX=0 StartY=33 StartZ=0 EndX=50 EndY=33 EndZ=0
    g11: LineSegment StartX=50 StartY=33 StartZ=0 EndX=50 EndY=22 EndZ=0
    g12: LineSegment StartX=50 StartY=22 StartZ=0 EndX=0 EndY=22 EndZ=0
    g13: LineSegment StartX=0 StartY=22 StartZ=0 EndX=0 EndY=20 EndZ=0
    g14: LineSegment StartX=-5 StartY=20 StartZ=0 EndX=-72.75 EndY=20 EndZ=0
  constraints (44):
    c: PointOnObject(g0,g-1)
    c: Coincident(g0,g1)
    c: PointOnObject(g1,g-1)
    c: Coincident(g1,g2)
    c: Coincident(g2,g3)
    c: Horizontal(g3)
    c: Coincident(g14,g4)
    c: Coincident(g4,g5)
    c: Coincident(g5,g0)
    c: Distance(g5) = 20
    c: Distance(g4) = 35.59
    c: Angle(g3,g4) = 2.0944
    c: Parallel(g4,g0)
    c: Perpendicular(g4,g5)
    c: PointOnObject(g6,g3)
    c: PointOnObject(g6,g-2)
    c: DistanceX(g14,g6) = 72.75
    c: DistanceX(g6,g2) = 80
    c: Vertical(g1,g2)
    c: DistanceY(g2,g2) = 20
    c: Vertical(g7)
    c: Coincident(g7,g8)
    c: PointOnObject(g8,g-2)
    c: Horizontal(g8)
    c: Coincident(g8,g9)
    c: PointOnObject(g9,g-2)
    c: Coincident(g9,g10)
    c: Horizontal(g10)
    c: Coincident(g10,g11)
    c: Coincident(g11,g12)
    c: PointOnObject(g12,g-2)
    c: Horizontal(g12)
    c: Coincident(g12,g13)
    c: Coincident(g13,g6)
    c: PointOnObject(g3,g13)
    c: Coincident(g14,g7)
    c: DistanceY(g13,g13) = 2
    c: DistanceY(g9,g9) = 2
    c: Horizontal(g3,g7)
    c: DistanceY(g7,g7) = 15
    c: Horizontal(g4,g7)
    c: DistanceX(g8,g8) = 5
    c: Vertical(g10,g11)
    c: DistanceX(g10,g10) = 50
FEATURE [PartDesign::SubShapeBinder] Binder
  BindCopyOnChange = 0
  BindMode = 0
  ClaimChildren = false
  Context = -> Body [Binder.]
  Fuse = false
  MakeFace = true
  OffsetFill = false
  OffsetIntersection = false
  OffsetJoinType = 0
  OffsetOpenResult = false
  PartialLoad = false
  Relative = true
  Support = -> [Sketch]
  _Version = 2
FEATURE [Sketcher::SketchObject] Sketch001
  ExternalGeometry = -> [Binder]
  FullyConstrained = true
  MapMode = 5
  Support = -> [XY_Plane]
  sketch-geometry (14):
    g0: LineSegment StartX=-90.545 StartY=50.8218 StartZ=0 EndX=-72.75 EndY=20 EndZ=0
    g1: LineSegment StartX=-72.75 StartY=20 StartZ=0 EndX=-5 EndY=20 EndZ=0
    g2: LineSegment StartX=-5 StartY=20 StartZ=0 EndX=-5 EndY=35 EndZ=0
    g3: LineSegment StartX=-5 StartY=35 StartZ=0 EndX=0 EndY=35 EndZ=0
    g4: LineSegment StartX=0 StartY=35 StartZ=0 EndX=0 EndY=33 EndZ=0
    g5: LineSegment StartX=0 StartY=33 StartZ=0 EndX=50 EndY=33 EndZ=0
    g6: LineSegment StartX=50 StartY=33 StartZ=0 EndX=50 EndY=22 EndZ=0
    g7: LineSegment StartX=50 StartY=22 StartZ=0 EndX=0 EndY=22 EndZ=0
    g8: LineSegment StartX=0 StartY=22 StartZ=0 EndX=0 EndY=20 EndZ=0
    g9: LineSegment StartX=0 StartY=20 StartZ=0 EndX=80 EndY=20 EndZ=0
    g10: LineSegment StartX=80 StartY=20 StartZ=0 EndX=80 EndY=0 EndZ=0
    g11: LineSegment StartX=80 StartY=0 StartZ=0 EndX=-84.297 EndY=0 EndZ=0
    g12: LineSegment StartX=-84.297 StartY=0 StartZ=0 EndX=-107.866 EndY=40.8218 EndZ=0
    g13: LineSegment StartX=-107.866 StartY=40.8218 StartZ=0 EndX=-90.545 EndY=50.8218 EndZ=0
  constraints (28):
    c: Coincident(g-15,g0)
    c: Coincident(g0,g-14)
    c: Coincident(g0,g1)
    c: Coincident(g1,g-13)
    c: Coincident(g1,g2)
    c: Coincident(g2,g-12)
    c: Coincident(g2,g3)
    c: Coincident(g3,g-11)
    c: Coincident(g3,g4)
    c: Coincident(g4,g-9)
    c: Coincident(g4,g5)
    c: Coincident(g5,g-10)
    c: Coincident(g5,g6)
    c: Coincident(g6,g-10)
    c: Coincident(g6,g7)
    c: Coincident(g7,g-8)
    c: Coincident(g7,g8)
    c: Coincident(g8,g-8)
    c: Coincident(g8,g9)
    c: Coincident(g9,g-6)
    c: Coincident(g9,g10)
    c: Coincident(g10,g-5)
    c: Coincident(g10,g11)
    c: Coincident(g11,g-4)
    c: Coincident(g11,g12)
    c: Coincident(g12,g-15)
    c: Coincident(g12,g13)
    c: Coincident(g13,g0)
FEATURE [PartDesign::Pad] Pad
  Direction = (0,0,1)
  Length = 13
  Length2 = 10
  Profile = -> Sketch001
  ReferenceAxis = -> Sketch001 [N_Axis]
  Type = 0
FEATURE [Sketcher::SketchObject] Sketch002
  ExternalGeometry = -> [Pad]
  FullyConstrained = true
  MapMode = 5
  Placement = pos=(0,0,0) rot=(1,0,0;3.14159rad)
  Support = -> [Pad]
  sketch-geometry (4):
    g0: LineSegment StartX=-84.297 StartY=0 StartZ=0 EndX=-72.75 EndY=-20 EndZ=0
    g1: LineSegment StartX=-72.75 StartY=-20 StartZ=0 EndX=-77.75 EndY=-28.6603 EndZ=0
    g2: LineSegment StartX=-77.75 StartY=-28.6603 StartZ=0 EndX=-89.297 EndY=-8.66025 EndZ=0
    g3: LineSegment StartX=-89.297 StartY=-8.66025 StartZ=0 EndX=-84.297 EndY=0 EndZ=0
  constraints (10):
    c: Coincident(g-3,g0)
    c: Coincident(g0,g-5)
    c: Coincident(g0,g1)
    c: PointOnObject(g1,g-5)
    c: Coincident(g1,g2)
    c: PointOnObject(g2,g-3)
    c: Coincident(g2,g3)
    c: Coincident(g3,g0)
    c: Equal(g3,g1)
    c: Distance(g3) = 10
FEATURE [PartDesign::Pad] Pad001
  BaseFeature = -> Pad
  Direction = (0,0,-1)
  Length = 13
  Length2 = 10
  Profile = -> Sketch002
  ReferenceAxis = -> Sketch002 [N_Axis]
  Type = 0
FEATURE [Sketcher::SketchObject] Sketch003
  ExternalGeometry = -> [Pad001]
  FullyConstrained = true
  MapMode = 5
  Placement = pos=(0,0,-13) rot=(1,0,0;3.14159rad)
  Support = -> [Pad001]
  sketch-geometry (4):
    g0: LineSegment StartX=-84.297 StartY=0 StartZ=0 EndX=-107.866 EndY=-40.8218 EndZ=0
    g1: LineSegment StartX=-107.866 StartY=-40.8218 StartZ=0 EndX=-90.545 EndY=-50.8218 EndZ=0
    g2: LineSegment StartX=-90.545 StartY=-50.8218 StartZ=0 EndX=-72.75 EndY=-20 EndZ=0
    g3: LineSegment StartX=-72.75 StartY=-20 StartZ=0 EndX=-84.297 EndY=0 EndZ=0
  constraints (8):
    c: Coincident(g-7,g0)
    c: Coincident(g0,g-5)
    c: Coincident(g0,g1)
    c: Coincident(g1,g-5)
    c: Coincident(g1,g2)
    c: Coincident(g2,g-6)
    c: Coincident(g2,g3)
    c: Coincident(g3,g0)
FEATURE [PartDesign::Pad] Pad002
  BaseFeature = -> Pad001
  Direction = (0,0,-1)
  Length = 13
  Length2 = 10
  Profile = -> Sketch003
  ReferenceAxis = -> Sketch003 [N_Axis]
  Type = 0
FEATURE [Sketcher::SketchObject] Sketch004
  ExternalGeometry = -> [Pad002]
  FullyConstrained = true
  MapMode = 5
  Placement = pos=(0,0,-26) rot=(1,0,0;3.14159rad)
  Support = -> [Pad002]
  sketch-geometry (5):
    g0: LineSegment StartX=-107.866 StartY=-40.8218 StartZ=0 EndX=-97.8655 EndY=-23.5013 EndZ=0
    g1: LineSegment StartX=-97.8655 StartY=-23.5013 StartZ=0 EndX=-80.545 EndY=-33.5013 EndZ=0
    g2: LineSegment StartX=-80.545 StartY=-33.5013 StartZ=0 EndX=-90.545 EndY=-50.8218 EndZ=0
    g3: LineSegment StartX=-90.545 StartY=-50.8218 StartZ=0 EndX=-107.866 EndY=-40.8218 EndZ=0
    g4: Circle CenterX=-94.2053 CenterY=-37.1616 CenterZ=0 NormalX=0 NormalY=0 NormalZ=1 AngleXU=0 Radius=6
  constraints (12):
    c: Coincident(g-4,g0)
    c: PointOnObject(g0,g-3)
    c: Coincident(g0,g1)
    c: PointOnObject(g1,g-5)
    c: Coincident(g1,g2)
    c: Coincident(g2,g-5)
    c: Coincident(g2,g3)
    c: Coincident(g3,g0)
    c: Parallel(g3,g1)
    c: Equal(g2,g3)
    c: Radius(g4) = 6
    c: Symmetric(g1,g0,g4)
FEATURE [PartDesign::Pocket] Pocket
  BaseFeature = -> Pad002
  Direction = (0,0,1)
  Length = 30
  Length2 = 5
  Profile = -> Sketch004
  ReferenceAxis = -> Sketch004 [N_Axis]
  Type = 1
FEATURE [Sketcher::SketchObject] Sketch005
  FullyConstrained = true
  MapMode = 5
  Placement = pos=(0,0,0) rot=(1,0,0;3.14159rad)
  Support = -> [Pocket]
FEATURE [Sketcher::SketchObject] Sketch006
  ExternalGeometry = -> [Pocket]
  FullyConstrained = true
  MapMode = 5
  Placement = pos=(50,0,0) rot=(0.57735,0.57735,0.57735;2.0944rad)
  Support = -> [Pocket]
  sketch-geometry (5):
    g0: LineSegment StartX=12.5 StartY=11.5 StartZ=0 EndX=12.5 EndY=1.5 EndZ=0
    g1: LineSegment StartX=12.5 StartY=1.5 StartZ=0 EndX=29.5 EndY=1.5 EndZ=0
    g2: LineSegment StartX=29.5 StartY=1.5 StartZ=0 EndX=29.5 EndY=11.5 EndZ=0
    g3: LineSegment StartX=29.5 StartY=11.5 StartZ=0 EndX=12.5 EndY=11.5 EndZ=0
    g4: GeomPoint X=21 Y=6.5 Z=0
  constraints (12):
    c: Coincident(g0,g1)
    c: Coincident(g1,g2)
    c: Coincident(g2,g3)
    c: Coincident(g3,g0)
    c: Horizontal(g1)
    c: Horizontal(g3)
    c: Vertical(g0)
    c: Vertical(g2)
    c: Symmetric(g1,g0,g4)
    c: Symmetric(g-4,g-6,g4)
    c: DistanceX(g3,g3) = 17
    c: DistanceY(g2,g2) = 10
FEATURE [PartDesign::Pocket] Pocket001
  BaseFeature = -> Pocket
  Direction = (-1,0,0)
  Length = 60
  Length2 = 5
  Profile = -> Sketch006
  ReferenceAxis = -> Sketch006 [N_Axis]
  Type = 0
FEATURE [PartDesign::CoordinateSystem] LCS_1
  AttacherType = Attacher::AttachEngine3D
  MapMode = 7
  Placement = pos=(0,22,1.5) rot=(0.57735,-0.57735,-0.57735;2.0944rad)
  Support = -> [Pocket001]
FEATURE [PartDesign::Body] Body
  Group = -> [Binder,Sketch001,Pad,Sketch002,Pad001,Sketch003,Pad002,Sketch004,Pocket,Sketch005,Sketch006,Pocket001,LCS_1]
  Origin = -> Origin
  Tip = -> Pocket001
---- part right_handle.FCStd = doc fcstd_666737c8c45f ----
FCSTD DOCUMENT  (FreeCAD 0.20R29177 +426 (Git))
Label: right_handle
License: All rights reserved
LicenseURL: http://en.wikipedia.org/wiki/All_rights_reserved
objects: Sketcher::SketchObject×6, PartDesign::Pad×4, PartDesign::SubShapeBinder×1, PartDesign::Pocket×1, PartDesign::CoordinateSystem×1, PartDesign::Body×1
note: 19 computed .brp shape members not serialized (recipe doc carries the construction recipe); baked Part::Feature solids carry a one-line shape summary decoded from their .brp

FEATURE [Sketcher::SketchObject] MirroredSketch  label="master_MirroredSketch"
  FullyConstrained = false
  sketch-geometry (15):
    g0: LineSegment StartX=-108.821 StartY=-42.476 StartZ=0 EndX=-84.297 EndY=0 EndZ=0
    g1: LineSegment StartX=-84.297 StartY=0 StartZ=0 EndX=80.003 EndY=0 EndZ=0
    g2: LineSegment StartX=80.003 StartY=0 StartZ=0 EndX=80.003 EndY=-20 EndZ=0
    g3: LineSegment StartX=80.003 StartY=-20 StartZ=0 EndX=0 EndY=-20 EndZ=0
    g4: LineSegment StartX=-72.75 StartY=-20 StartZ=0 EndX=-91.5 EndY=-52.476 EndZ=0
    g5: LineSegment StartX=-91.5 StartY=-52.476 StartZ=0 EndX=-108.821 EndY=-42.476 EndZ=0
    g6: GeomPoint X=0 Y=-20 Z=0
    g7: LineSegment StartX=-5 StartY=-20 StartZ=0 EndX=-5 EndY=-35 EndZ=0
    g8: LineSegment StartX=-5 StartY=-35 StartZ=0 EndX=0 EndY=-35 EndZ=0
    g9: LineSegment StartX=0 StartY=-35 StartZ=0 EndX=0 EndY=-33 EndZ=0
    g10: LineSegment StartX=0 StartY=-33 StartZ=0 EndX=50 EndY=-33 EndZ=0
    g11: LineSegment StartX=50 StartY=-33 StartZ=0 EndX=50 EndY=-22 EndZ=0
    g12: LineSegment StartX=50 StartY=-22 StartZ=0 EndX=0 EndY=-22 EndZ=0
    g13: LineSegment StartX=0 StartY=-22 StartZ=0 EndX=0 EndY=-20 EndZ=0
    g14: LineSegment StartX=-5 StartY=-20 StartZ=0 EndX=-72.75 EndY=-20 EndZ=0
  constraints (37):
    c: Coincident(g0,g1)
    c: Coincident(g1,g2)
    c: Coincident(g2,g3)
    c: Horizontal(g3)
    c: Coincident(g14,g4)
    c: Coincident(g4,g5)
    c: Coincident(g5,g0)
    c: Distance(g5) = 20
    c: Distance(g4) = 37.5
    c: Angle(g3,g4) = -2.0944
    c: Parallel(g4,g0)
    c: Perpendicular(g4,g5)
    c: PointOnObject(g6,g3)
    c: Vertical(g7)
    c: Coincident(g7,g8)
    c: Horizontal(g8)
    c: Coincident(g8,g9)
    c: Coincident(g9,g10)
    c: Horizontal(g10)
    c: Coincident(g10,g11)
    c: Coincident(g11,g12)
    c: Horizontal(g12)
    c: Coincident(g12,g13)
    c: Coincident(g13,g6)
    c: PointOnObject(g3,g13)
    c: Coincident(g14,g7)
    c: Horizontal(g14)
    c: Horizontal(g7,g3)
    c: DistanceY(g7,g7) = 15
    c: DistanceY(g2,g2) = 20
    c: Horizontal(g1)
    c: PointOnObject(g0,g-1)
    c: DistanceX(g1,g1) = 164.3
    c: Vertical(g2)
    c: DistanceX(g14,g14) = 67.75
    c: DistanceX(g8,g8) = 5
    c: PointOnObject(g8,g-2)
FEATURE [PartDesign::SubShapeBinder] Binder
  BindCopyOnChange = 0
  BindMode = 0
  ClaimChildren = false
  Context = -> Body [Binder.]
  Fuse = false
  MakeFace = true
  OffsetFill = false
  OffsetIntersection = false
  OffsetJoinType = 0
  OffsetOpenResult = false
  PartialLoad = false
  Relative = true
  Support = -> [MirroredSketch]
  _Version = 2
FEATURE [Sketcher::SketchObject] Sketch
  ExternalGeometry = -> [Binder]
  FullyConstrained = true
  MapMode = 5
  Support = -> [XY_Plane]
  sketch-geometry (14):
    g0: LineSegment StartX=-84.297 StartY=0 StartZ=0 EndX=80.003 EndY=0 EndZ=0
    g1: LineSegment StartX=80.003 StartY=0 StartZ=0 EndX=80.003 EndY=-20 EndZ=0
    g2: LineSegment StartX=80.003 StartY=-20 StartZ=0 EndX=0 EndY=-20 EndZ=0
    g3: LineSegment StartX=0 StartY=-20 StartZ=0 EndX=0 EndY=-22 EndZ=0
    g4: LineSegment StartX=0 StartY=-22 StartZ=0 EndX=50 EndY=-22 EndZ=0
    g5: LineSegment StartX=50 StartY=-22 StartZ=0 EndX=50 EndY=-33 EndZ=0
    g6: LineSegment StartX=50 StartY=-33 StartZ=0 EndX=0 EndY=-33 EndZ=0
    g7: LineSegment StartX=0 StartY=-33 StartZ=0 EndX=0 EndY=-35 EndZ=0
    g8: LineSegment StartX=0 StartY=-35 StartZ=0 EndX=-5 EndY=-35 EndZ=0
    g9: LineSegment StartX=-5 StartY=-35 StartZ=0 EndX=-5 EndY=-20 EndZ=0
    g10: LineSegment StartX=-5 StartY=-20 StartZ=0 EndX=-72.75 EndY=-20 EndZ=0
    g11: LineSegment StartX=-72.75 StartY=-20 StartZ=0 EndX=-77.75 EndY=-28.6603 EndZ=0
    g12: LineSegment StartX=-77.75 StartY=-28.6603 StartZ=0 EndX=-89.297 EndY=-8.66025 EndZ=0
    g13: LineSegment StartX=-89.297 StartY=-8.66025 StartZ=0 EndX=-84.297 EndY=0 EndZ=0
  constraints (30):
    c: Coincident(g-12,g0)
    c: Coincident(g0,g-13)
    c: Coincident(g0,g1)
    c: Coincident(g1,g-13)
    c: Coincident(g1,g2)
    c: Coincident(g2,g-6)
    c: Coincident(g2,g3)
    c: Coincident(g3,g-6)
    c: Coincident(g3,g4)
    c: Coincident(g4,g-7)
    c: Coincident(g4,g5)
    c: Coincident(g5,g-8)
    c: Coincident(g5,g6)
    c: Coincident(g6,g-9)
    c: Coincident(g6,g7)
    c: Coincident(g7,g-10)
    c: Coincident(g7,g8)
    c: Coincident(g8,g-11)
    c: Coincident(g8,g9)
    c: Coincident(g9,g-11)
    c: Coincident(g9,g10)
    c: Coincident(g10,g-3)
    c: Coincident(g10,g11)
    c: Coincident(g11,g12)
    c: Coincident(g12,g13)
    c: Coincident(g13,g0)
    c: PointOnObject(g11,g-15)
    c: PointOnObject(g12,g-14)
    c: Equal(g11,g13)
    c: Distance(g11) = 10
FEATURE [PartDesign::Pad] Pad
  Direction = (0,0,1)
  Length = 13
  Length2 = 10
  Profile = -> Sketch
  ReferenceAxis = -> Sketch [N_Axis]
  Type = 0
FEATURE [Sketcher::SketchObject] Sketch001
  ExternalGeometry = -> [Binder]
  FullyConstrained = true
  MapMode = 5
  Placement = pos=(0,0,13) rot=(0,0,1;0rad)
  Support = -> [Pad]
  sketch-geometry (4):
    g0: LineSegment StartX=-84.297 StartY=0 StartZ=0 EndX=-72.75 EndY=-20 EndZ=0
    g1: LineSegment StartX=-72.75 StartY=-20 StartZ=0 EndX=-91.5 EndY=-52.476 EndZ=0
    g2: LineSegment StartX=-91.5 StartY=-52.476 StartZ=0 EndX=-108.821 EndY=-42.476 EndZ=0
    g3: LineSegment StartX=-108.821 StartY=-42.476 StartZ=0 EndX=-84.297 EndY=0 EndZ=0
  constraints (8):
    c: Coincident(g-3,g0)
    c: Coincident(g0,g-4)
    c: Coincident(g0,g1)
    c: Coincident(g1,g-5)
    c: Coincident(g1,g2)
    c: Coincident(g2,g-5)
    c: Coincident(g2,g3)
    c: Coincident(g3,g0)
FEATURE [PartDesign::Pad] Pad001
  BaseFeature = -> Pad
  Direction = (0,0,1)
  Length = 13
  Length2 = 10
  Profile = -> Sketch001
  ReferenceAxis = -> Sketch001 [N_Axis]
  Type = 0
FEATURE [Sketcher::SketchObject] Sketch002
  ExternalGeometry = -> [Pad001]
  FullyConstrained = true
  MapMode = 5
  Placement = pos=(0,0,0) rot=(1,0,0;3.14159rad)
  Support = -> [Pad001]
  sketch-geometry (4):
    g0: LineSegment StartX=-77.75 StartY=28.6603 StartZ=0 EndX=-89.297 EndY=8.66025 EndZ=0
    g1: LineSegment StartX=-89.297 StartY=8.66025 StartZ=0 EndX=-84.297 EndY=0 EndZ=0
    g2: LineSegment StartX=-84.297 StartY=0 StartZ=0 EndX=-72.75 EndY=20 EndZ=0
    g3: LineSegment StartX=-72.75 StartY=20 StartZ=0 EndX=-77.75 EndY=28.6603 EndZ=0
  constraints (8):
    c: Coincident(g-4,g0)
    c: Coincident(g0,g-5)
    c: Coincident(g0,g1)
    c: Coincident(g1,g-5)
    c: Coincident(g1,g2)
    c: Coincident(g2,g-3)
    c: Coincident(g2,g3)
    c: Coincident(g3,g0)
FEATURE [PartDesign::Pad] Pad002
  BaseFeature = -> Pad001
  Direction = (0,0,-1)
  Length = 26
  Length2 = 10
  Profile = -> Sketch002
  ReferenceAxis = -> Sketch002 [N_Axis]
  Type = 0
FEATURE [Sketcher::SketchObject] Sketch003
  ExternalGeometry = -> [Pad002]
  FullyConstrained = true
  MapMode = 5
  Placement = pos=(0,0,-26) rot=(1,0,0;3.14159rad)
  Support = -> [Pad002]
  sketch-geometry (4):
    g0: LineSegment StartX=-72.75 StartY=20 StartZ=0 EndX=-91.5 EndY=52.476 EndZ=0
    g1: LineSegment StartX=-91.5 StartY=52.476 StartZ=0 EndX=-108.821 EndY=42.476 EndZ=0
    g2: LineSegment StartX=-108.821 StartY=42.476 StartZ=0 EndX=-84.297 EndY=0 EndZ=0
    g3: LineSegment StartX=-84.297 StartY=0 StartZ=0 EndX=-72.75 EndY=20 EndZ=0
  constraints (8):
    c: Coincident(g-8,g0)
    c: Coincident(g0,g-4)
    c: Coincident(g0,g1)
    c: Coincident(g1,g-5)
    c: Coincident(g1,g2)
    c: Coincident(g2,g-8)
    c: Coincident(g2,g3)
    c: Coincident(g3,g0)
FEATURE [PartDesign::Pad] Pad003
  BaseFeature = -> Pad002
  Direction = (0,0,-1)
  Length = 13
  Length2 = 10
  Profile = -> Sketch003
  ReferenceAxis = -> Sketch003 [N_Axis]
  Type = 0
FEATURE [Sketcher::SketchObject] Sketch004
  ExternalGeometry = -> [Pad003]
  FullyConstrained = true
  MapMode = 5
  Placement = pos=(0,0,-39) rot=(1,0,0;3.14159rad)
  Support = -> [Pad003]
  sketch-geometry (5):
    g0: LineSegment StartX=-81.5 StartY=35.1554 StartZ=0 EndX=-91.5 EndY=52.476 EndZ=0
    g1: LineSegment StartX=-91.5 StartY=52.476 StartZ=0 EndX=-108.821 EndY=42.476 EndZ=0
    g2: LineSegment StartX=-108.821 StartY=42.476 StartZ=0 EndX=-98.8205 EndY=25.1554 EndZ=0
    g3: LineSegment StartX=-98.8205 StartY=25.1554 StartZ=0 EndX=-81.5 EndY=35.1554 EndZ=0
    g4: Circle CenterX=-95.1603 CenterY=38.8157 CenterZ=0 NormalX=0 NormalY=0 NormalZ=1 AngleXU=0 Radius=6
  constraints (12):
    c: PointOnObject(g0,g-4)
    c: Coincident(g0,g-5)
    c: Coincident(g0,g1)
    c: Coincident(g1,g-5)
    c: Coincident(g1,g2)
    c: PointOnObject(g2,g-3)
    c: Coincident(g2,g3)
    c: Coincident(g3,g0)
    c: Parallel(g3,g1)
    c: Equal(g0,g1)
    c: Symmetric(g0,g2,g4)
    c: Radius(g4) = 6
FEATURE [PartDesign::Pocket] Pocket
  BaseFeature = -> Pad003
  Direction = (0,0,1)
  Length = 54
  Length2 = 5
  Profile = -> Sketch004
  ReferenceAxis = -> Sketch004 [N_Axis]
  Type = 0
FEATURE [PartDesign::CoordinateSystem] LCS_1
  AttacherType = Attacher::AttachEngine3D
  MapMode = 7
  Placement = pos=(0,-33,0) rot=(0,1,0;3.14159rad)
  Support = -> [Pocket]
FEATURE [PartDesign::Body] Body
  Group = -> [Binder,Sketch,Pad,Sketch001,Pad001,Sketch002,Pad002,Sketch003,Pad003,Sketch004,Pocket,LCS_1]
  Origin = -> Origin
  Tip = -> Pocket
